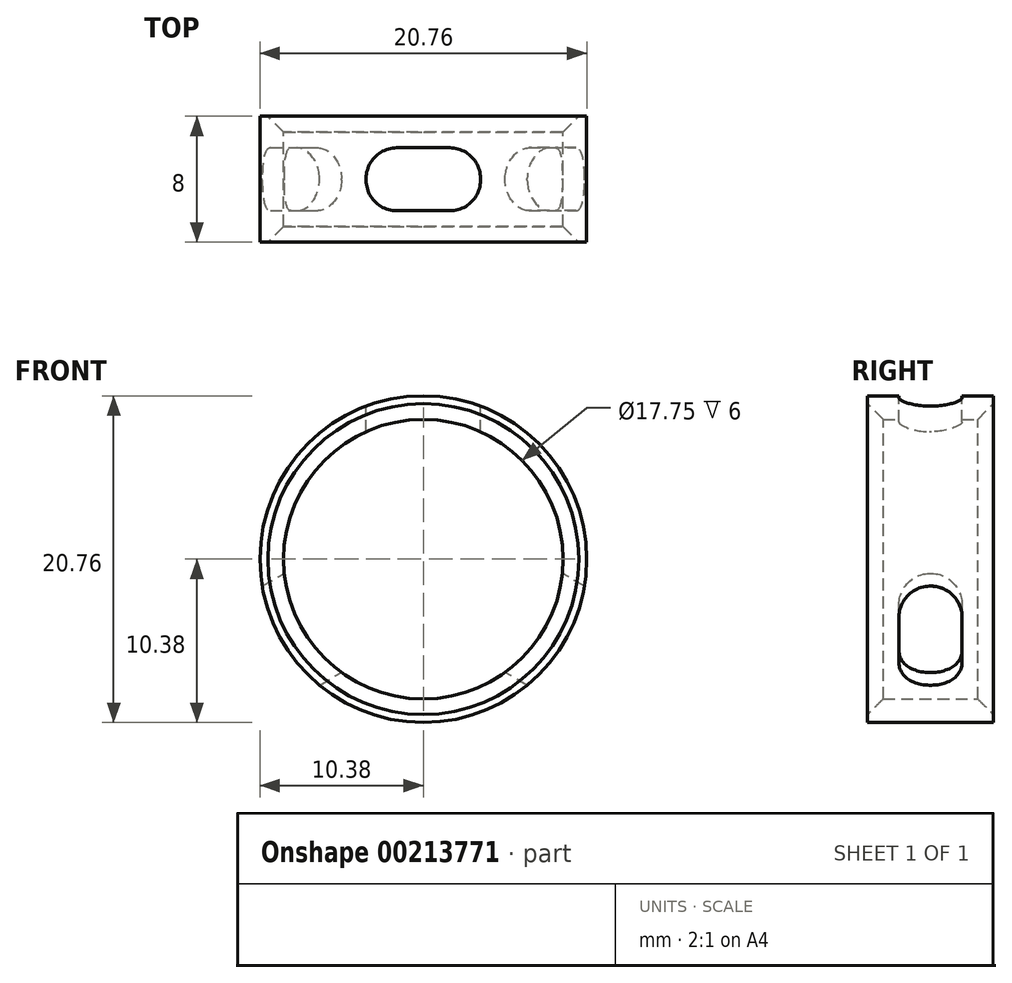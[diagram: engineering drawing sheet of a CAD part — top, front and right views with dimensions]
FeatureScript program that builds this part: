
annotation { "Feature Type Name" : "Feature", "Feature Type Description" : "" }
export const myFeature = defineFeature(function(context is Context, id is Id, definition is map)
    precondition{}
    {
        {
            var Q0;
            Q0=qCreatedBy(makeId("Front.planeOp"),FACE);
            var sketch = newSketch(context, id + "F0", { "sketchPlane" : qUnion([Q0])});
            skCircle(sketch, "E0", {"center": v(0, 0) * mm, "radius": 8.88 * mm});
            skCircle(sketch, "E1.0", {"center": v(0, 0) * mm, "radius": 10.38 * mm});
            skLineSegment(sketch, "E2.bottom", {"start": v(3.63, 9.72) * mm, "end": v(-3.63, 9.72) * mm, "construction": true});
            skLineSegment(sketch, "E2.top", {"start": v(3.63, 11.88) * mm, "end": v(-3.63, 11.88) * mm});
            skLineSegment(sketch, "E2.left", {"start": v(3.63, 9.72) * mm, "end": v(3.63, 11.88) * mm});
            skLineSegment(sketch, "E2.right", {"start": v(-3.63, 9.72) * mm, "end": v(-3.63, 11.88) * mm});
            skPoint(sketch, "E2.middle", {"position": v(0, 10.8) * mm});
            skLineSegment(sketch, "E3.1.0", {"start": v(-6.6, -8) * mm, "end": v(-8.47, -9.08) * mm});
            skLineSegment(sketch, "E3.1.1", {"start": v(-10.23, -1.71) * mm, "end": v(-12.1, -2.8) * mm});
            skLineSegment(sketch, "E3.1.2", {"start": v(-12.1, -2.8) * mm, "end": v(-8.47, -9.08) * mm});
            skLineSegment(sketch, "E3.1.3", {"start": v(-10.23, -1.71) * mm, "end": v(-6.6, -8) * mm, "construction": true});
            skLineSegment(sketch, "E3.2.0", {"start": v(10.23, -1.71) * mm, "end": v(12.1, -2.8) * mm});
            skLineSegment(sketch, "E3.2.1", {"start": v(6.6, -8) * mm, "end": v(8.47, -9.08) * mm});
            skLineSegment(sketch, "E3.2.2", {"start": v(8.47, -9.08) * mm, "end": v(12.1, -2.8) * mm});
            skLineSegment(sketch, "E3.2.3", {"start": v(6.6, -8) * mm, "end": v(10.23, -1.71) * mm, "construction": true});
            skLineSegment(sketch, "E4", {"start": v(0, 0) * mm, "end": v(7.34, 7.34) * mm, "construction": true});
            skLineSegment(sketch, "E5", {"start": v(0, 0) * mm, "end": v(-7.34, 7.34) * mm, "construction": true});
            skLineSegment(sketch, "E6.MirrorCS", {"start": v(0, 0) * mm, "end": v(7.34, -7.34) * mm, "construction": true});
            skLineSegment(sketch, "E7.MirrorCS", {"start": v(0, 0) * mm, "end": v(-7.34, -7.34) * mm, "construction": true});
            skLineSegment(sketch, "E8.0", {"start": v(-0.14, 0.14) * mm, "end": v(0, 0.28) * mm});
            skLineSegment(sketch, "E9.MirrorCS", {"start": v(0.14, -0.14) * mm, "end": v(0.28, 0) * mm});
            skLineSegment(sketch, "E10.MirrorCS", {"start": v(0.14, 0.14) * mm, "end": v(0, 0.28) * mm});
            skLineSegment(sketch, "E11.MirrorCS", {"start": v(-0.14, -0.14) * mm, "end": v(-0.28, 0) * mm});
            skLineSegment(sketch, "E12.MirrorCS", {"start": v(0.14, 0.14) * mm, "end": v(0.28, 0) * mm});
            skLineSegment(sketch, "E13.MirrorCS", {"start": v(-0.14, -0.14) * mm, "end": v(0, -0.28) * mm});
            skLineSegment(sketch, "E14.MirrorCS", {"start": v(0.14, -0.14) * mm, "end": v(0, -0.28) * mm});
            skLineSegment(sketch, "E15.MirrorCS", {"start": v(-0.14, 0.14) * mm, "end": v(-0.28, 0) * mm});
            skLineSegment(sketch, "E16.trimOffspring", {"start": v(-6.13, -6.42) * mm, "end": v(-7.2, -7.48) * mm, "construction": true});
            skLineSegment(sketch, "E17.trimOffspring", {"start": v(-6.42, -6.13) * mm, "end": v(-7.48, -7.2) * mm, "construction": true});
            skLineSegment(sketch, "E18.trimOffspring", {"start": v(-6.42, 6.13) * mm, "end": v(-7.48, 7.2) * mm, "construction": true});
            skLineSegment(sketch, "E19.trimOffspring", {"start": v(-6.13, 6.42) * mm, "end": v(-7.2, 7.48) * mm, "construction": true});
            skLineSegment(sketch, "E20.trimOffspring", {"start": v(6.13, 6.42) * mm, "end": v(7.2, 7.48) * mm, "construction": true});
            skLineSegment(sketch, "E21.trimOffspring", {"start": v(6.42, 6.13) * mm, "end": v(7.48, 7.2) * mm, "construction": true});
            skLineSegment(sketch, "E22.trimOffspring", {"start": v(6.13, -6.42) * mm, "end": v(7.2, -7.48) * mm, "construction": true});
            skLineSegment(sketch, "E23.trimOffspring", {"start": v(6.42, -6.13) * mm, "end": v(7.48, -7.2) * mm, "construction": true});
            skLineSegment(sketch, "E24", {"start": v(-3.63, 9.72) * mm, "end": v(-3.63, 6.6) * mm});
            skLineSegment(sketch, "E25", {"start": v(-3.63, 6.6) * mm, "end": v(3.63, 6.6) * mm});
            skLineSegment(sketch, "E26", {"start": v(3.63, 6.6) * mm, "end": v(3.63, 9.72) * mm});
            skLineSegment(sketch, "E27", {"start": v(10.23, -1.71) * mm, "end": v(7.27, 0) * mm});
            skLineSegment(sketch, "E28", {"start": v(6.6, -8) * mm, "end": v(3.35, -6.13) * mm});
            skLineSegment(sketch, "E29", {"start": v(3.35, -6.13) * mm, "end": v(7.27, 0) * mm});
            skLineSegment(sketch, "E30", {"start": v(-6.6, -8) * mm, "end": v(-3.28, -6.1) * mm});
            skLineSegment(sketch, "E31", {"start": v(-10.23, -1.71) * mm, "end": v(-6.86, 0.24) * mm});
            skLineSegment(sketch, "E32", {"start": v(-6.86, 0.24) * mm, "end": v(-3.28, -6.1) * mm});
            skSolve(sketch);
        }
        {
            var Q0;
            Q0=makeQuery(id+"F0.imprint","IMPRINT",FACE,{"disambiguationData":[TD([[makeQuery(id+"F0.imprint","IMPRINT",EDGE,{"derivedFrom":sQuery(id+"F0.wireOp",EDGE,"E0")}),-1.0]])]});
            var Q1;
            {var subQ2=sQuery(id+"F0.wireOp",EDGE,"E16.trimOffspring");var subQ7=sQuery(id+"F0.wireOp",EDGE,"E0");var subQ9=makeQuery(id+"F0.imprint","INTERSECT",VERTEX,{"derivedFrom":[subQ7,subQ2]});Q1=makeQuery(id+"F0.imprint","IMPRINT",FACE,{"disambiguationData":[TD([[makeQuery(id+"F0.imprint","IMPRINT",EDGE,{"disambiguationData":[TD([[subQ9,-1.0]])],"derivedFrom":subQ7}),-1.0]])]});}
            var Q2;
            {var subQ5=sQuery(id+"F0.wireOp",EDGE,"E21.trimOffspring");var subQ7=sQuery(id+"F0.wireOp",EDGE,"E0");var subQ8=makeQuery(id+"F0.imprint","INTERSECT",VERTEX,{"derivedFrom":[subQ7,subQ5]});Q2=makeQuery(id+"F0.imprint","IMPRINT",FACE,{"disambiguationData":[TD([[makeQuery(id+"F0.imprint","IMPRINT",EDGE,{"disambiguationData":[TD([[subQ8,1.0]])],"derivedFrom":subQ7}),-1.0]])]});}
            var Q3;
            {var subQ2=sQuery(id+"F0.wireOp",EDGE,"E19.trimOffspring");var subQ7=sQuery(id+"F0.wireOp",EDGE,"E0");var subQ8=makeQuery(id+"F0.imprint","INTERSECT",VERTEX,{"derivedFrom":[subQ7,subQ2]});Q3=makeQuery(id+"F0.imprint","IMPRINT",FACE,{"disambiguationData":[TD([[makeQuery(id+"F0.imprint","IMPRINT",EDGE,{"disambiguationData":[TD([[subQ8,1.0]])],"derivedFrom":subQ7}),-1.0]])]});}
            var Q4;
            {var subQ5=sQuery(id+"F0.wireOp",EDGE,"E17.trimOffspring");var subQ6=sQuery(id+"F0.wireOp",EDGE,"E0");var subQ7=makeQuery(id+"F0.imprint","INTERSECT",VERTEX,{"derivedFrom":[subQ6,subQ5]});Q4=makeQuery(id+"F0.imprint","IMPRINT",FACE,{"disambiguationData":[TD([[makeQuery(id+"F0.imprint","IMPRINT",EDGE,{"disambiguationData":[TD([[subQ7,1.0]])],"derivedFrom":subQ6}),-1.0]])]});}
            extrude(context, id + "F1", {"entities" : qUnion([Q0, Q1, Q2, Q3, Q4]), "depth" : 4 * mm, "hasSecondDirection" : true, "secondDirectionOppositeDirection" : true, "secondDirectionDepth" : 4 * mm});
        }
        {
            var Q0;
            Q0=makeQuery(id+"F1.opExtrude","CAP_EDGE",EDGE,{"disambiguationData":[OSD([sQuery(id+"F0.wireOp",EDGE,"E0")])],"isStart":false});
            var Q1;
            Q1=makeQuery(id+"F1.opExtrude","CAP_EDGE",EDGE,{"disambiguationData":[OSD([sQuery(id+"F0.wireOp",EDGE,"E0")])],"isStart":true});
            chamfer(context, id + "F2", {"entities" : qUnion([Q0, Q1]), "width" : 1 * mm, "tangentPropagation" : true});
        }
        {
            var Q0;
            Q0=qCreatedBy(makeId("Top.planeOp"),FACE);
            var sketch = newSketch(context, id + "F3", { "sketchPlane" : qUnion([Q0])});
            skCircle(sketch, "E33", {"center": v(0, 0) * mm, "radius": 0.15 * mm});
            skCircle(sketch, "E34.1.0.0", {"center": v(0, -0.6) * mm, "radius": 0.15 * mm});
            skCircle(sketch, "E34.2.0.0", {"center": v(0, -1.2) * mm, "radius": 0.15 * mm});
            skCircle(sketch, "E34.3.0.0", {"center": v(0, -1.8) * mm, "radius": 0.15 * mm});
            skCircle(sketch, "E34.4.0.0", {"center": v(0, -2.4) * mm, "radius": 0.15 * mm});
            skCircle(sketch, "E34.5.0.0", {"center": v(0, -3) * mm, "radius": 0.15 * mm});
            skCircle(sketch, "E34.6.0.0", {"center": v(0, -3.6) * mm, "radius": 0.15 * mm});
            skLineSegment(sketch, "E34.direction1", {"start": v(0, 0) * mm, "end": v(0, -0.6) * mm, "construction": true});
            skCircle(sketch, "E35.MirrorC", {"center": v(0, 0.6) * mm, "radius": 0.15 * mm});
            skCircle(sketch, "E36.MirrorC", {"center": v(0, 1.2) * mm, "radius": 0.15 * mm});
            skCircle(sketch, "E37.MirrorC", {"center": v(0, 1.8) * mm, "radius": 0.15 * mm});
            skCircle(sketch, "E38.MirrorC", {"center": v(0, 2.4) * mm, "radius": 0.15 * mm});
            skCircle(sketch, "E39.MirrorC", {"center": v(0, 3) * mm, "radius": 0.15 * mm});
            skCircle(sketch, "E40.MirrorC", {"center": v(0, 3.6) * mm, "radius": 0.15 * mm});
            skSolve(sketch);
        }
        {
            var Q0;
            Q0=makeQuery(id+"F0.imprint","IMPRINT",FACE,{"disambiguationData":[TD([[makeQuery(id+"F0.imprint","IMPRINT",EDGE,{"derivedFrom":sQuery(id+"F0.wireOp",EDGE,"E2.top")}),1.0]])]});
            var Q1;
            {var subQ0=sQuery(id+"F0.wireOp",EDGE,"E24");var subQ1=sQuery(id+"F0.wireOp",EDGE,"E0");var subQ2=makeQuery(id+"F0.imprint","INTERSECT",VERTEX,{"derivedFrom":[subQ1,subQ0]});Q1=makeQuery(id+"F0.imprint","IMPRINT",FACE,{"disambiguationData":[TD([[makeQuery(id+"F0.imprint","IMPRINT",EDGE,{"disambiguationData":[TD([[subQ2,1.0]])],"derivedFrom":subQ1}),-1.0]])]});}
            var Q2;
            {var subQ5=sQuery(id+"F0.wireOp",EDGE,"E25");Q2=makeQuery(id+"F0.imprint","IMPRINT",FACE,{"disambiguationData":[TD([[makeQuery(id+"F0.imprint","IMPRINT",EDGE,{"derivedFrom":subQ5}),1.0]])]});}
            var Q3;
            {var subQ5=sQuery(id+"F0.wireOp",EDGE,"E29");Q3=makeQuery(id+"F0.imprint","IMPRINT",FACE,{"disambiguationData":[TD([[makeQuery(id+"F0.imprint","IMPRINT",EDGE,{"derivedFrom":subQ5}),-1.0]])]});}
            var Q4;
            {var subQ0=sQuery(id+"F0.wireOp",EDGE,"E28");var subQ1=sQuery(id+"F0.wireOp",EDGE,"E0");var subQ2=makeQuery(id+"F0.imprint","INTERSECT",VERTEX,{"derivedFrom":[subQ1,subQ0]});Q4=makeQuery(id+"F0.imprint","IMPRINT",FACE,{"disambiguationData":[TD([[makeQuery(id+"F0.imprint","IMPRINT",EDGE,{"disambiguationData":[TD([[subQ2,-1.0]])],"derivedFrom":subQ1}),-1.0]])]});}
            var Q5;
            {var subQ0=sQuery(id+"F0.wireOp",EDGE,"E3.2.0");Q5=makeQuery(id+"F0.imprint","IMPRINT",FACE,{"disambiguationData":[TD([[makeQuery(id+"F0.imprint","IMPRINT",EDGE,{"derivedFrom":subQ0}),-1.0]])]});}
            var Q6;
            {var subQ5=sQuery(id+"F0.wireOp",EDGE,"E32");Q6=makeQuery(id+"F0.imprint","IMPRINT",FACE,{"disambiguationData":[TD([[makeQuery(id+"F0.imprint","IMPRINT",EDGE,{"derivedFrom":subQ5}),-1.0]])]});}
            var Q7;
            {var subQ0=sQuery(id+"F0.wireOp",EDGE,"E3.1.0");Q7=makeQuery(id+"F0.imprint","IMPRINT",FACE,{"disambiguationData":[TD([[makeQuery(id+"F0.imprint","IMPRINT",EDGE,{"derivedFrom":subQ0}),-1.0]])]});}
            var Q8;
            {var subQ0=sQuery(id+"F0.wireOp",EDGE,"E31");var subQ1=sQuery(id+"F0.wireOp",EDGE,"E0");var subQ2=makeQuery(id+"F0.imprint","INTERSECT",VERTEX,{"derivedFrom":[subQ1,subQ0]});Q8=makeQuery(id+"F0.imprint","IMPRINT",FACE,{"disambiguationData":[TD([[makeQuery(id+"F0.imprint","IMPRINT",EDGE,{"disambiguationData":[TD([[subQ2,-1.0]])],"derivedFrom":subQ1}),-1.0]])]});}
            extrude(context, id + "F4", {"entities" : qUnion([Q0, Q1, Q2, Q3, Q4, Q5, Q6, Q7, Q8]), "operationType" : NewBodyOperationType.REMOVE, "oppositeDirection" : true, "depth" : 2 * mm, "hasSecondDirection" : true, "secondDirectionOppositeDirection" : false, "secondDirectionDepth" : 2 * mm});
        }
        {
            var Q0;
            Q0=makeQuery(id+"F4.boolean.opBoolean","COPY",EDGE,{"derivedFrom":makeQuery(id+"F4.opExtrude","CAP_EDGE",EDGE,{"disambiguationData":[OSD([sQuery(id+"F0.wireOp",EDGE,"E3.2.1"),sQuery(id+"F0.wireOp",EDGE,"E28")])],"isStart":false})});
            var Q1;
            Q1=makeQuery(id+"F4.boolean.opBoolean","COPY",EDGE,{"derivedFrom":makeQuery(id+"F4.opExtrude","CAP_EDGE",EDGE,{"disambiguationData":[OSD([sQuery(id+"F0.wireOp",EDGE,"E3.2.0"),sQuery(id+"F0.wireOp",EDGE,"E27")])],"isStart":false})});
            var Q2;
            Q2=makeQuery(id+"F4.boolean.opBoolean","COPY",EDGE,{"derivedFrom":makeQuery(id+"F4.opExtrude","CAP_EDGE",EDGE,{"disambiguationData":[OSD([sQuery(id+"F0.wireOp",EDGE,"E3.2.0"),sQuery(id+"F0.wireOp",EDGE,"E27")])],"isStart":true})});
            var Q3;
            Q3=makeQuery(id+"F4.boolean.opBoolean","COPY",EDGE,{"derivedFrom":makeQuery(id+"F4.opExtrude","CAP_EDGE",EDGE,{"disambiguationData":[OSD([sQuery(id+"F0.wireOp",EDGE,"E3.2.1"),sQuery(id+"F0.wireOp",EDGE,"E28")])],"isStart":true})});
            var Q4;
            Q4=makeQuery(id+"F4.boolean.opBoolean","COPY",EDGE,{"derivedFrom":makeQuery(id+"F4.opExtrude","CAP_EDGE",EDGE,{"disambiguationData":[OSD([sQuery(id+"F0.wireOp",EDGE,"E3.1.0"),sQuery(id+"F0.wireOp",EDGE,"E30")])],"isStart":false})});
            var Q5;
            Q5=makeQuery(id+"F4.boolean.opBoolean","COPY",EDGE,{"derivedFrom":makeQuery(id+"F4.opExtrude","CAP_EDGE",EDGE,{"disambiguationData":[OSD([sQuery(id+"F0.wireOp",EDGE,"E3.1.1"),sQuery(id+"F0.wireOp",EDGE,"E31")])],"isStart":false})});
            var Q6;
            Q6=makeQuery(id+"F4.boolean.opBoolean","COPY",EDGE,{"derivedFrom":makeQuery(id+"F4.opExtrude","CAP_EDGE",EDGE,{"disambiguationData":[OSD([sQuery(id+"F0.wireOp",EDGE,"E3.1.1"),sQuery(id+"F0.wireOp",EDGE,"E31")])],"isStart":true})});
            var Q7;
            Q7=makeQuery(id+"F4.boolean.opBoolean","COPY",EDGE,{"derivedFrom":makeQuery(id+"F4.opExtrude","CAP_EDGE",EDGE,{"disambiguationData":[OSD([sQuery(id+"F0.wireOp",EDGE,"E3.1.0"),sQuery(id+"F0.wireOp",EDGE,"E30")])],"isStart":true})});
            var Q8;
            Q8=makeQuery(id+"F4.boolean.opBoolean","COPY",EDGE,{"derivedFrom":makeQuery(id+"F4.opExtrude","CAP_EDGE",EDGE,{"disambiguationData":[OSD([sQuery(id+"F0.wireOp",EDGE,"E2.right"),sQuery(id+"F0.wireOp",EDGE,"E24")])],"isStart":false})});
            var Q9;
            Q9=makeQuery(id+"F4.boolean.opBoolean","COPY",EDGE,{"derivedFrom":makeQuery(id+"F4.opExtrude","CAP_EDGE",EDGE,{"disambiguationData":[OSD([sQuery(id+"F0.wireOp",EDGE,"E2.left"),sQuery(id+"F0.wireOp",EDGE,"E26")])],"isStart":false})});
            var Q10;
            Q10=makeQuery(id+"F4.boolean.opBoolean","COPY",EDGE,{"derivedFrom":makeQuery(id+"F4.opExtrude","CAP_EDGE",EDGE,{"disambiguationData":[OSD([sQuery(id+"F0.wireOp",EDGE,"E2.right"),sQuery(id+"F0.wireOp",EDGE,"E24")])],"isStart":true})});
            var Q11;
            Q11=makeQuery(id+"F4.boolean.opBoolean","COPY",EDGE,{"derivedFrom":makeQuery(id+"F4.opExtrude","CAP_EDGE",EDGE,{"disambiguationData":[OSD([sQuery(id+"F0.wireOp",EDGE,"E2.left"),sQuery(id+"F0.wireOp",EDGE,"E26")])],"isStart":true})});
            fillet(context, id + "F5", {"entities" : qUnion([Q0, Q1, Q2, Q3, Q4, Q5, Q6, Q7, Q8, Q9, Q10, Q11]), "radius" : 1.94 * mm, "tangentPropagation" : true, "allowEdgeOverflow" : false});
        }
    });
